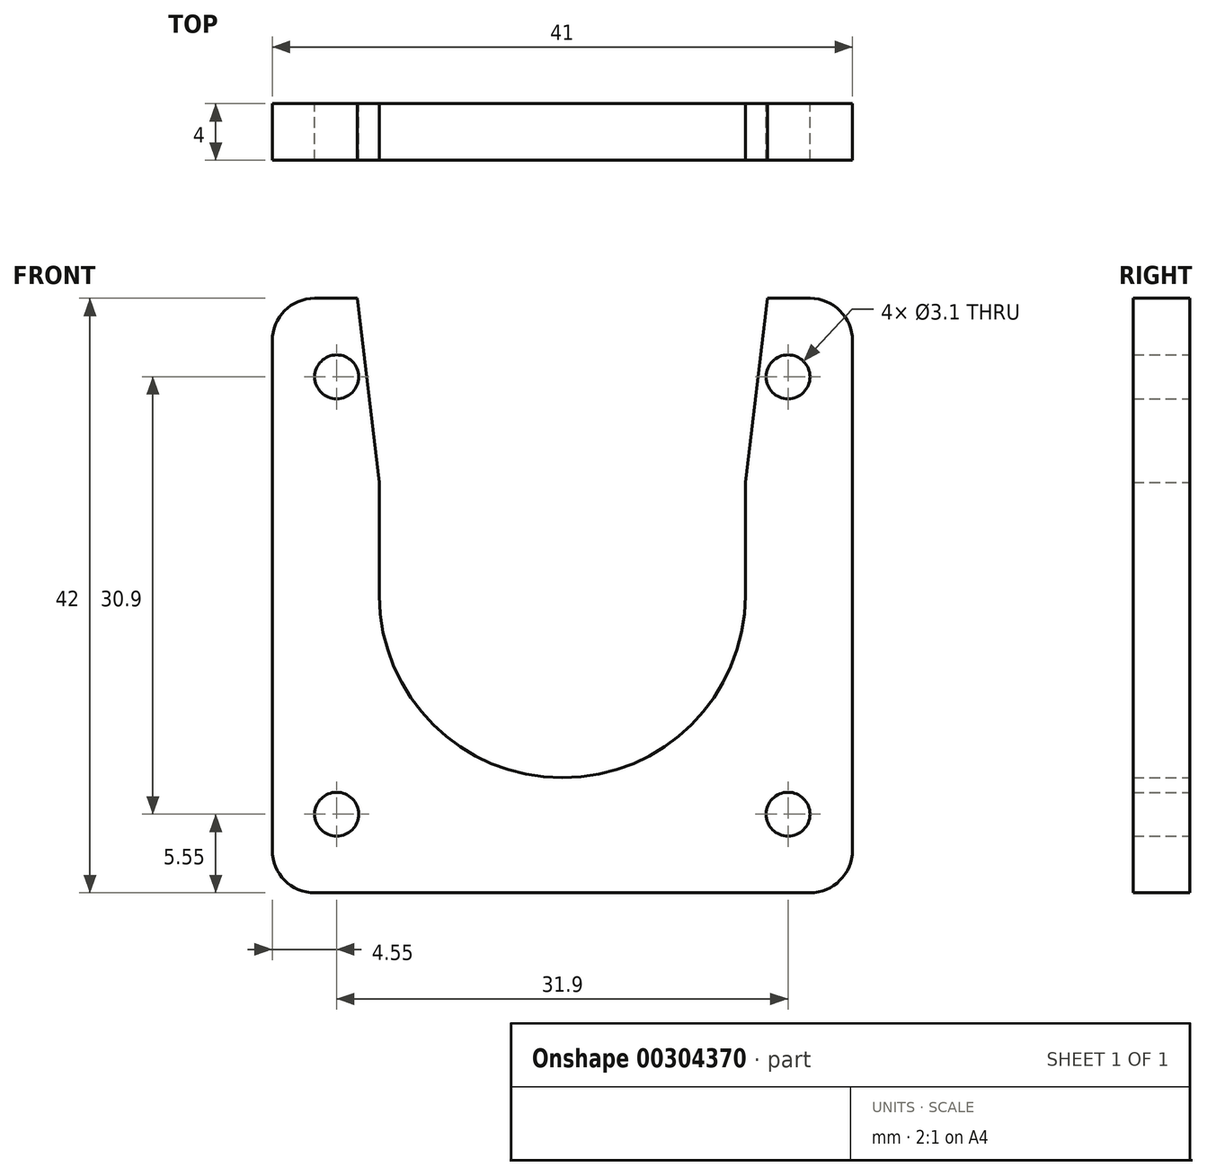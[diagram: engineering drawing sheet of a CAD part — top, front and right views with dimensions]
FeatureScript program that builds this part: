
annotation { "Feature Type Name" : "Feature", "Feature Type Description" : "" }
export const myFeature = defineFeature(function(context is Context, id is Id, definition is map)
    precondition{}
    {
        {
            var Q0;
            Q0=qCreatedBy(makeId("Front.planeOp"),FACE);
            var sketch = newSketch(context, id + "F0", { "sketchPlane" : qUnion([Q0])});
            skLineSegment(sketch, "E0.bottom", {"start": v(-17.5, 21) * mm, "end": v(-14.5, 21) * mm});
            skLineSegment(sketch, "E0.top", {"start": v(-17.5, -21) * mm, "end": v(17.5, -21) * mm});
            skLineSegment(sketch, "E0.left", {"start": v(-20.5, 18) * mm, "end": v(-20.5, -18) * mm});
            skLineSegment(sketch, "E0.right", {"start": v(20.5, 18) * mm, "end": v(20.5, -18) * mm});
            skLineSegment(sketch, "E1", {"start": v(-12.94, 8) * mm, "end": v(-12.94, 0) * mm});
            skLineSegment(sketch, "E2", {"start": v(-14.5, 21) * mm, "end": v(-12.94, 8) * mm});
            skLineSegment(sketch, "E3.MirrorCS", {"start": v(14.5, 21) * mm, "end": v(12.94, 8) * mm});
            skLineSegment(sketch, "E4.MirrorCS", {"start": v(12.94, 8) * mm, "end": v(12.94, 0) * mm});
            skArc(sketch, "E5", {"start": v(-12.94, 0) * mm, "mid": v(0, -12.88) * mm, "end": v(12.94, 0) * mm});
            skPoint(sketch, "E6.orphan", {"position": v(-12.94, -7.6) * mm});
            skPoint(sketch, "E7.orphan", {"position": v(12.94, -7.6) * mm});
            skLineSegment(sketch, "E8.trimOffspring", {"start": v(14.5, 21) * mm, "end": v(17.5, 21) * mm});
            skCircle(sketch, "E9", {"center": v(-15.95, -15.45) * mm, "radius": 1.55 * mm});
            skCircle(sketch, "E10.MirrorC", {"center": v(-15.95, 15.45) * mm, "radius": 1.55 * mm});
            skCircle(sketch, "E11.MirrorC", {"center": v(15.95, 15.45) * mm, "radius": 1.55 * mm});
            skCircle(sketch, "E12.MirrorC", {"center": v(15.95, -15.45) * mm, "radius": 1.55 * mm});
            skPoint(sketch, "E13.visualSharp", {"position": v(-20.5, 21) * mm});
            skArc(sketch, "E13.filletArc", {"start": v(-17.5, 21) * mm, "mid": v(-19.62, 20.12) * mm, "end": v(-20.5, 18) * mm});
            skPoint(sketch, "E14.visualSharp", {"position": v(20.5, 21) * mm});
            skArc(sketch, "E14.filletArc", {"start": v(20.5, 18) * mm, "mid": v(19.62, 20.12) * mm, "end": v(17.5, 21) * mm});
            skPoint(sketch, "E15.visualSharp", {"position": v(20.5, -21) * mm});
            skArc(sketch, "E15.filletArc", {"start": v(17.5, -21) * mm, "mid": v(19.62, -20.12) * mm, "end": v(20.5, -18) * mm});
            skPoint(sketch, "E16.visualSharp", {"position": v(-20.5, -21) * mm});
            skArc(sketch, "E16.filletArc", {"start": v(-20.5, -18) * mm, "mid": v(-19.62, -20.12) * mm, "end": v(-17.5, -21) * mm});
            skSolve(sketch);
        }
        {
            var Q0;
            Q0 = qSketchRegion(id + "F0", true);
            extrude(context, id + "F1", {"entities" : qUnion([Q0]), "depth" : 4 * mm});
        }
    });
